# Revit family: Drain_Floor_Square_Hinged_9_Inch_Diameter_Zurn-Z513-Heavy-Duty
name_source: partatom
category: Plumbing Fixtures
units: mm (PartAtom-declared; Revit-internal decimal feet)

## family parameters
Always vertical = Yes
Cut with Voids When Loaded = No
Maintain Annotation Orientation = No
OmniClass Number = 23.45.55.21
OmniClass Title = Drains (Wastes)
Part Type = Normal
Room Calculation Point = No
Round Connector Dimension = Use Radius
Shared = No
Work Plane-Based = No

## types (4) — shared parameters
Approx. Wt.Lbs. = 57 "
Assembly Code = D2030300
B = 1.736 "
Bottom Plate Width = 13.375 "
CW Connection = No
Description = 9 [229] SQUARE HINGED HEAVY-DUTY DRAIN
Grate Open Area Sq. In = 20 "
Grate Width = 7.5 "
HW Connection = No
Main Material = Iron - Zurn - Cast - Painted - Blue
Manufacturer = Zurn Water, LLC
Manufacturer Brand = Zurn
Model = Z513
Modified Date = 12/12/2025
Product Documentation Link = https://files.zurn.com
Product Page URL = https://www.zurn.com
Product data URL = https://www.bimobject.com
URL = www.zurn.com
Vent Connection = No
WFU = 1
Waste Connection = Yes
Width = 9 "
zero-valued in all types: CWFU, HWFU

## per-type parameters (varying)
| type | Default Elevation | Grate Material | Grate width | Pipe Size_A Inside Radius | Pipe Size_A Nominal Radius | Pipe Size_A Outer Radius | ZN_Frame Height | ZN_Top | ZN_Top Visibility |
| Z513-3 Inch Neo-Loc Outlet | 20 " | Iron - Zurn - Cast - Painted - Blue | 7.5 " | 1.534 " | 1.5 " | 1.75 " | 2.313 " | 9 " | No |
| Z513-4 Inch Neo-Loc Outlet | 0 " | Iron - Zurn - Cast - Painted - Blue | 7.5 " | 2.013 " | 2 " | 2.25 " | 2.313 " | 9 " | No |
| ZN513-3 Inch Neo-Loc Outlet | 0 " | Bronze - Zurn - Polished Nickel | 7.5 " | 1.534 " | 1.5 " | 1.75 " | 2.5 " | 9.75 " | Yes |
| ZN513-4 Inch Neo-Loc Outlet | 0 " | Bronze - Zurn - Polished Nickel | 8.375 " | 2.013 " | 2 " | 2.25 " | 2.5 " | 9.75 " | Yes |

## geometry (parser evidence)
native form markers: Blend x6, Sweep x6
no freeform markers — native parametric forms only
